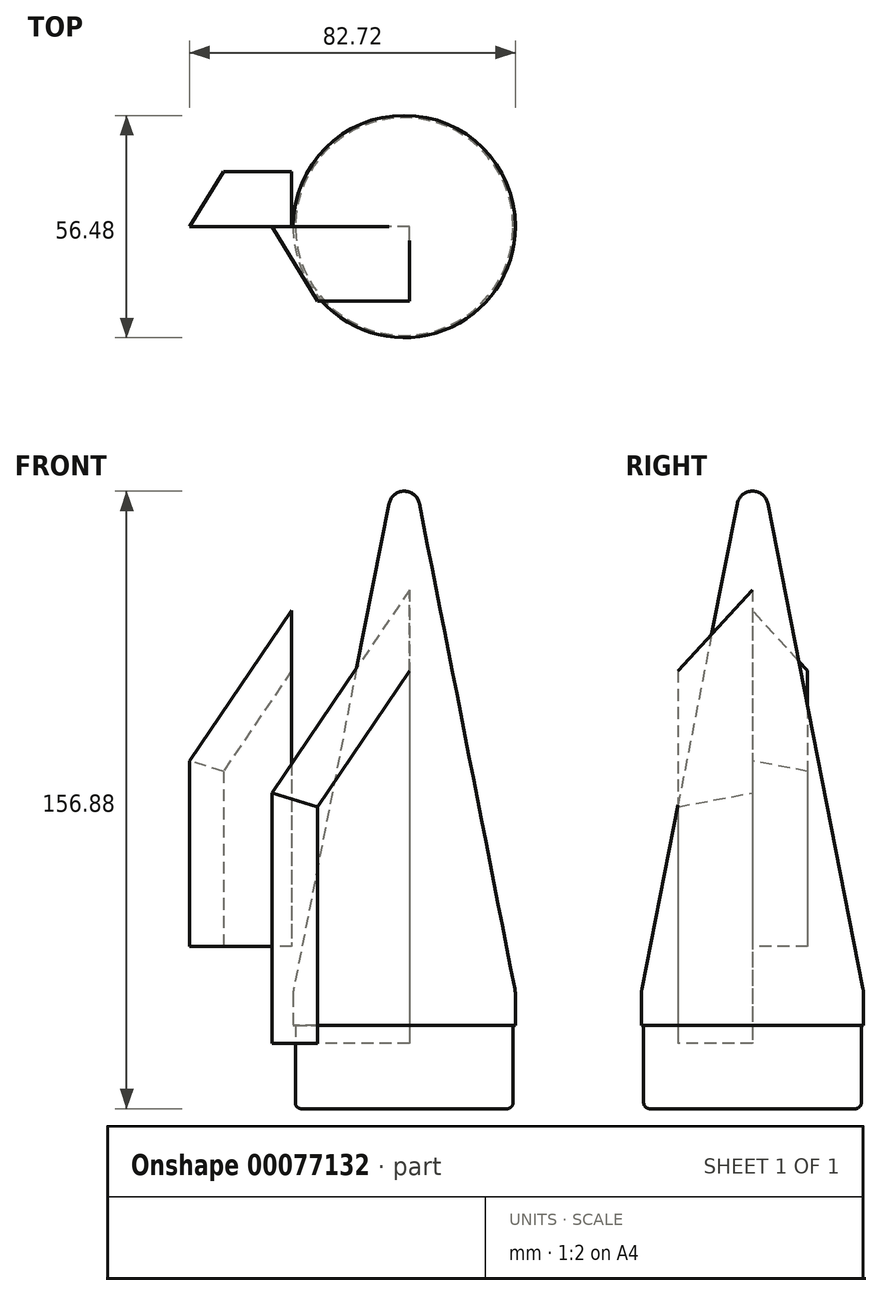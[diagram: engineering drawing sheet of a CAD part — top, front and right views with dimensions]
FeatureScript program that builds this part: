
annotation { "Feature Type Name" : "Feature", "Feature Type Description" : "" }
export const myFeature = defineFeature(function(context is Context, id is Id, definition is map)
    precondition{}
    {
        {
            var Q0;
            Q0=qCreatedBy(makeId("Front.planeOp"),FACE);
            var sketch = newSketch(context, id + "F0", { "sketchPlane" : qUnion([Q0])});
            skLineSegment(sketch, "E0", {"start": v(-33.3, -70.07) * mm, "end": v(-33.3, -70.07) * mm});
            skLineSegment(sketch, "E1", {"start": v(0, -70.07) * mm, "end": v(0, 79.93) * mm});
            skLineSegment(sketch, "E2", {"start": v(0, -70.07) * mm, "end": v(0, -80.07) * mm});
            skLineSegment(sketch, "E3", {"start": v(-32.6, -80.07) * mm, "end": v(-33.3, -80.07) * mm});
            skLineSegment(sketch, "E4", {"start": v(-33.3, -80.07) * mm, "end": v(-33.3, -70.07) * mm});
            skPoint(sketch, "E5.orphan", {"position": v(0, 86.63) * mm});
            skLineSegment(sketch, "E6", {"start": v(-33.3, -70.07) * mm, "end": v(-4.56, 76.18) * mm});
            skLineSegment(sketch, "E7.top", {"start": v(0, -105.07) * mm, "end": v(-32.6, -105.07) * mm});
            skLineSegment(sketch, "E7.left", {"start": v(0, -80.07) * mm, "end": v(0, -105.07) * mm});
            skLineSegment(sketch, "E7.right", {"start": v(-32.6, -80.07) * mm, "end": v(-32.6, -105.07) * mm});
            skArc(sketch, "E8", {"start": v(0, 79.93) * mm, "mid": v(-2.95, 78.87) * mm, "end": v(-4.56, 76.18) * mm});
            skSolve(sketch);
        }
        {
            var Q0;
            {var subQ0=sQuery(id+"F0.wireOp",EDGE,"E2");Q0=makeQuery(id+"F0.imprint","IMPRINT",FACE,{"disambiguationData":[TD([[makeQuery(id+"F0.imprint","IMPRINT",EDGE,{"derivedFrom":subQ0}),-1.0]])]});}
            var Q1;
            Q1=sQuery(id+"F0.wireOp",EDGE,"E1");
            revolve(context, id + "F1", {"entities" : qUnion([Q0]), "axis" : qUnion([Q1]), "revolveType" : RevolveType.FULL});
        }
        {
            var Q0;
            Q0=makeQuery(id+"F1.opRevolve","SWEPT_BODY",BODY,{"disambiguationData":[OSD([sQuery(id+"F0.wireOp",EDGE,"Oh61cgLR-RQo2-T4aV-TcRg-Gp7ijPdUG9jl"),sQuery(id+"F0.wireOp",EDGE,"E1"),sQuery(id+"F0.wireOp",EDGE,"E2"),sQuery(id+"F0.wireOp",EDGE,"E3"),sQuery(id+"F0.wireOp",EDGE,"E4"),sQuery(id+"F0.wireOp",EDGE,"E0"),sQuery(id+"F0.wireOp",EDGE,"dTV1AxgJ-VMAe-DLQO-Zqz3-4UbtDb8FiUJC")])]});
            var Q1;
            Q1=qCreatedBy(makeId("Origin.pointOp"),VERTEX);
            transform(context, id + "F2", {"entities" : qUnion([Q0]), "transformType" : TransformType.SCALE_UNIFORMLY, "scale" : .848, "scalePoint" : qUnion([Q1]), "makeCopy" : false});
        }
        {
            var Q0;
            Q0=qCreatedBy(makeId("Front.planeOp"),FACE);
            var sketch = newSketch(context, id + "F3", { "sketchPlane" : qUnion([Q0])});
            skLineSegment(sketch, "E9", {"start": v(-56.93, -47.9) * mm, "end": v(-56.93, 0) * mm});
            skLineSegment(sketch, "E10", {"start": v(-56.93, 0) * mm, "end": v(-28.6, 41.78) * mm});
            skLineSegment(sketch, "E11", {"start": v(-28.6, 41.78) * mm, "end": v(-28.6, -47.9) * mm});
            skLineSegment(sketch, "E12", {"start": v(-28.6, -47.9) * mm, "end": v(-56.93, -47.9) * mm});
            skSolve(sketch);
        }
        {
            var Q0;
            Q0=makeQuery(id+"F3.imprint","IMPRINT",FACE,{"disambiguationData":[TD([[makeQuery(id+"F3.imprint","IMPRINT",EDGE,{"derivedFrom":sQuery(id+"F3.wireOp",EDGE,"E9")}),-1.0]])]});
            extrude(context, id + "F4", {"entities" : qUnion([Q0]), "depth" : 14 * mm, "offsetDistance" : 25 * mm});
        }
        {
            var Q0;
            Q0=makeQuery(id+"F4.opExtrude","CAP_EDGE",EDGE,{"disambiguationData":[OSD([sQuery(id+"F3.wireOp",EDGE,"E10")])],"isStart":false});
            var Q1;
            Q1=makeQuery(id+"F4.opExtrude","CAP_EDGE",EDGE,{"disambiguationData":[OSD([sQuery(id+"F3.wireOp",EDGE,"E9")])],"isStart":false});
            chamfer(context, id + "F5", {"entities" : qUnion([Q0, Q1]), "chamferType" : ChamferType.TWO_OFFSETS, "width1" : 11 * mm, "oppositeDirection" : false, "width2" : 18 * mm, "tangentPropagation" : true});
        }
        {
            var Q0;
            Q0=makeQuery(id+"F4.opExtrude","SWEPT_BODY",BODY,{"disambiguationData":[OSD([sQuery(id+"F3.wireOp",EDGE,"E9"),sQuery(id+"F3.wireOp",EDGE,"E10"),sQuery(id+"F3.wireOp",EDGE,"E11"),sQuery(id+"F3.wireOp",EDGE,"E12")])]});
            var Q1;
            Q1=qCreatedBy(makeId("Front.planeOp"),FACE);
            mirror(context, id + "F6", {"operationType" : NewBodyOperationType.ADD, "entities" : qUnion([Q0]), "mirrorPlane" : qUnion([Q1])});
        }
        {
            var Q0;
            Q0=makeQuery(id+"F4.opExtrude","SWEPT_BODY",BODY,{"disambiguationData":[OSD([sQuery(id+"F3.wireOp",EDGE,"E9"),sQuery(id+"F3.wireOp",EDGE,"E10"),sQuery(id+"F3.wireOp",EDGE,"E11"),sQuery(id+"F3.wireOp",EDGE,"E12")])]});
            transform(context, id + "F7", {"entities" : qUnion([Q0]), "transformType" : TransformType.TRANSLATION_3D, "dx" : 29.6 * mm, "dy" : 0 * mm, "dz" : -5.8 * mm, "makeCopy" : false});
        }
        {
            var Q0;
            Q0=makeQuery(id+"F1.opRevolve","SWEPT_EDGE",EDGE,{"disambiguationData":[OSD([sQuery(id+"F0.wireOp",EDGE,"E4"),sQuery(id+"F0.wireOp",EDGE,"E6")])]});
            fillet(context, id + "F8", {"entities" : qUnion([Q0]), "radius" : 7.8 * mm, "tangentPropagation" : true, "allowEdgeOverflow" : false});
        }
        {
            var Q0;
            Q0=makeQuery(id+"F1.opRevolve","SWEPT_EDGE",EDGE,{"disambiguationData":[OSD([sQuery(id+"F0.wireOp",EDGE,"E7.top"),sQuery(id+"F0.wireOp",EDGE,"E7.right")])]});
            fillet(context, id + "F9", {"entities" : qUnion([Q0]), "radius" : 1.5 * mm, "tangentPropagation" : true, "allowEdgeOverflow" : false});
        }
        {
            var Q0;
            Q0=qCreatedBy(makeId("Top.planeOp"),FACE);
            cPlane(context, id + "F10", {"entities" : qUnion([Q0]), "cplaneType" : CPlaneType.OFFSET, "offset" : 25 * mm, "oppositeDirection" : true, "width" : 150 * mm, "height" : 150 * mm});
        }
        {
            var Q0;
            Q0=qCreatedBy(makeId("Front.planeOp"),FACE);
            cPlane(context, id + "F11", {"entities" : qUnion([Q0]), "cplaneType" : CPlaneType.OFFSET, "offset" : 35 * mm, "width" : 150 * mm, "height" : 150 * mm});
        }
        {
            var Q0;
            Q0=qCreatedBy(id+"F11.planeOp",FACE);
            var sketch = newSketch(context, id + "F12", { "sketchPlane" : qUnion([Q0])});
            skText(sketch, "E13", { "text": "DC3Dparts", "fontName": "OpenSans-Regular.ttf"});
            const initialGuessF12  = {"E13": [-0.024, -0.07859, 1, 0, 0.007]};
            skSetInitialGuess(sketch, initialGuessF12);
            skSolve(sketch);
        }
        {
            var Q0;
            Q0=qSketchRegion(id+"F12",true);
            var Q1;
            Q1=qCreatedBy(makeId("Front.planeOp"),FACE);
            extrude(context, id + "F13", {"entities" : qUnion([Q0]), "endBound" : BoundingType.UP_TO_SURFACE, "oppositeDirection" : true, "depth" : 25 * mm, "endBoundEntityFace" : qUnion([Q1]), "offsetDistance" : 25 * mm});
        }
        {
            var Q0;
            Q0=qCreatedBy(makeId("Front.planeOp"),FACE);
            var sketch = newSketch(context, id + "F14", { "sketchPlane" : qUnion([Q0])});
            skLineSegment(sketch, "E14.bottom", {"start": v(0, -64.71) * mm, "end": v(-27, -64.71) * mm});
            skLineSegment(sketch, "E14.top", {"start": v(0, -103.72) * mm, "end": v(-27, -103.72) * mm});
            skLineSegment(sketch, "E14.left", {"start": v(0, -64.71) * mm, "end": v(0, -103.72) * mm});
            skLineSegment(sketch, "E14.right", {"start": v(-27, -64.71) * mm, "end": v(-27, -103.72) * mm});
            skSolve(sketch);
        }
        {
            var Q0;
            Q0=makeQuery(id+"F14.imprint","IMPRINT",FACE,{"disambiguationData":[TD([[makeQuery(id+"F14.imprint","IMPRINT",EDGE,{"derivedFrom":sQuery(id+"F14.wireOp",EDGE,"E14.bottom")}),1.0]])]});
            var Q1;
            Q1=sQuery(id+"F14.wireOp",EDGE,"E14.left");
            revolve(context, id + "F15", {"entities" : qUnion([Q0]), "axis" : qUnion([Q1]), "revolveType" : RevolveType.FULL});
        }
        {
            var Q0;
            Q0=makeQuery(id+"F15.opRevolve","SWEPT_BODY",BODY,{"disambiguationData":[OSD([sQuery(id+"F14.wireOp",EDGE,"E14.bottom"),sQuery(id+"F14.wireOp",EDGE,"E14.top"),sQuery(id+"F14.wireOp",EDGE,"E14.left"),sQuery(id+"F14.wireOp",EDGE,"E14.right")])]});
            var Q1;
            Q1=makeQuery(id+"F13.opExtrude","SWEPT_BODY",BODY,{"disambiguationData":[OSD([sQuery(id+"F12.wireOp",EDGE,"E13.sketch_text.stroke-0"),sQuery(id+"F12.wireOp",EDGE,"E13.sketch_text.stroke-1"),sQuery(id+"F12.wireOp",EDGE,"E13.sketch_text.stroke-2"),sQuery(id+"F12.wireOp",EDGE,"E13.sketch_text.stroke-3"),sQuery(id+"F12.wireOp",EDGE,"E13.sketch_text.stroke-4"),sQuery(id+"F12.wireOp",EDGE,"E13.sketch_text.stroke-5"),sQuery(id+"F12.wireOp",EDGE,"E13.sketch_text.stroke-6"),sQuery(id+"F12.wireOp",EDGE,"E13.sketch_text.stroke-7"),sQuery(id+"F12.wireOp",EDGE,"E13.sketch_text.stroke-8"),sQuery(id+"F12.wireOp",EDGE,"E13.sketch_text.stroke-9"),sQuery(id+"F12.wireOp",EDGE,"E13.sketch_text.stroke-10"),sQuery(id+"F12.wireOp",EDGE,"E13.sketch_text.stroke-11"),sQuery(id+"F12.wireOp",EDGE,"E13.sketch_text.stroke-12"),sQuery(id+"F12.wireOp",EDGE,"E13.sketch_text.stroke-13")])]});
            var Q2;
            Q2=makeQuery(id+"F13.opExtrude","SWEPT_BODY",BODY,{"disambiguationData":[OSD([sQuery(id+"F12.wireOp",EDGE,"E13.sketch_text.stroke-14"),sQuery(id+"F12.wireOp",EDGE,"E13.sketch_text.stroke-15"),sQuery(id+"F12.wireOp",EDGE,"E13.sketch_text.stroke-16"),sQuery(id+"F12.wireOp",EDGE,"E13.sketch_text.stroke-17"),sQuery(id+"F12.wireOp",EDGE,"E13.sketch_text.stroke-18"),sQuery(id+"F12.wireOp",EDGE,"E13.sketch_text.stroke-19"),sQuery(id+"F12.wireOp",EDGE,"E13.sketch_text.stroke-20"),sQuery(id+"F12.wireOp",EDGE,"E13.sketch_text.stroke-21"),sQuery(id+"F12.wireOp",EDGE,"E13.sketch_text.stroke-22"),sQuery(id+"F12.wireOp",EDGE,"E13.sketch_text.stroke-23"),sQuery(id+"F12.wireOp",EDGE,"E13.sketch_text.stroke-24"),sQuery(id+"F12.wireOp",EDGE,"E13.sketch_text.stroke-25"),sQuery(id+"F12.wireOp",EDGE,"E13.sketch_text.stroke-26"),sQuery(id+"F12.wireOp",EDGE,"E13.sketch_text.stroke-27"),sQuery(id+"F12.wireOp",EDGE,"E13.sketch_text.stroke-28")])]});
            var Q3;
            Q3=makeQuery(id+"F13.opExtrude","SWEPT_BODY",BODY,{"disambiguationData":[OSD([sQuery(id+"F12.wireOp",EDGE,"E13.sketch_text.stroke-29"),sQuery(id+"F12.wireOp",EDGE,"E13.sketch_text.stroke-30"),sQuery(id+"F12.wireOp",EDGE,"E13.sketch_text.stroke-31"),sQuery(id+"F12.wireOp",EDGE,"E13.sketch_text.stroke-32"),sQuery(id+"F12.wireOp",EDGE,"E13.sketch_text.stroke-33"),sQuery(id+"F12.wireOp",EDGE,"E13.sketch_text.stroke-34"),sQuery(id+"F12.wireOp",EDGE,"E13.sketch_text.stroke-35"),sQuery(id+"F12.wireOp",EDGE,"E13.sketch_text.stroke-36"),sQuery(id+"F12.wireOp",EDGE,"E13.sketch_text.stroke-37"),sQuery(id+"F12.wireOp",EDGE,"E13.sketch_text.stroke-38"),sQuery(id+"F12.wireOp",EDGE,"E13.sketch_text.stroke-39"),sQuery(id+"F12.wireOp",EDGE,"E13.sketch_text.stroke-40"),sQuery(id+"F12.wireOp",EDGE,"E13.sketch_text.stroke-41"),sQuery(id+"F12.wireOp",EDGE,"E13.sketch_text.stroke-42"),sQuery(id+"F12.wireOp",EDGE,"E13.sketch_text.stroke-43"),sQuery(id+"F12.wireOp",EDGE,"E13.sketch_text.stroke-44"),sQuery(id+"F12.wireOp",EDGE,"E13.sketch_text.stroke-45"),sQuery(id+"F12.wireOp",EDGE,"E13.sketch_text.stroke-46"),sQuery(id+"F12.wireOp",EDGE,"E13.sketch_text.stroke-47"),sQuery(id+"F12.wireOp",EDGE,"E13.sketch_text.stroke-48"),sQuery(id+"F12.wireOp",EDGE,"E13.sketch_text.stroke-49"),sQuery(id+"F12.wireOp",EDGE,"E13.sketch_text.stroke-50"),sQuery(id+"F12.wireOp",EDGE,"E13.sketch_text.stroke-51"),sQuery(id+"F12.wireOp",EDGE,"E13.sketch_text.stroke-52"),sQuery(id+"F12.wireOp",EDGE,"E13.sketch_text.stroke-53"),sQuery(id+"F12.wireOp",EDGE,"E13.sketch_text.stroke-54"),sQuery(id+"F12.wireOp",EDGE,"E13.sketch_text.stroke-55"),sQuery(id+"F12.wireOp",EDGE,"E13.sketch_text.stroke-56")])]});
            var Q4;
            Q4=makeQuery(id+"F13.opExtrude","SWEPT_BODY",BODY,{"disambiguationData":[OSD([sQuery(id+"F12.wireOp",EDGE,"E13.sketch_text.stroke-57"),sQuery(id+"F12.wireOp",EDGE,"E13.sketch_text.stroke-58"),sQuery(id+"F12.wireOp",EDGE,"E13.sketch_text.stroke-59"),sQuery(id+"F12.wireOp",EDGE,"E13.sketch_text.stroke-60"),sQuery(id+"F12.wireOp",EDGE,"E13.sketch_text.stroke-61"),sQuery(id+"F12.wireOp",EDGE,"E13.sketch_text.stroke-62"),sQuery(id+"F12.wireOp",EDGE,"E13.sketch_text.stroke-63"),sQuery(id+"F12.wireOp",EDGE,"E13.sketch_text.stroke-64"),sQuery(id+"F12.wireOp",EDGE,"E13.sketch_text.stroke-65"),sQuery(id+"F12.wireOp",EDGE,"E13.sketch_text.stroke-66"),sQuery(id+"F12.wireOp",EDGE,"E13.sketch_text.stroke-67"),sQuery(id+"F12.wireOp",EDGE,"E13.sketch_text.stroke-68"),sQuery(id+"F12.wireOp",EDGE,"E13.sketch_text.stroke-69"),sQuery(id+"F12.wireOp",EDGE,"E13.sketch_text.stroke-70")])]});
            var Q5;
            Q5=makeQuery(id+"F13.opExtrude","SWEPT_BODY",BODY,{"disambiguationData":[OSD([sQuery(id+"F12.wireOp",EDGE,"E13.sketch_text.stroke-71"),sQuery(id+"F12.wireOp",EDGE,"E13.sketch_text.stroke-72"),sQuery(id+"F12.wireOp",EDGE,"E13.sketch_text.stroke-73"),sQuery(id+"F12.wireOp",EDGE,"E13.sketch_text.stroke-74"),sQuery(id+"F12.wireOp",EDGE,"E13.sketch_text.stroke-75"),sQuery(id+"F12.wireOp",EDGE,"E13.sketch_text.stroke-76"),sQuery(id+"F12.wireOp",EDGE,"E13.sketch_text.stroke-77"),sQuery(id+"F12.wireOp",EDGE,"E13.sketch_text.stroke-78"),sQuery(id+"F12.wireOp",EDGE,"E13.sketch_text.stroke-79"),sQuery(id+"F12.wireOp",EDGE,"E13.sketch_text.stroke-80"),sQuery(id+"F12.wireOp",EDGE,"E13.sketch_text.stroke-81"),sQuery(id+"F12.wireOp",EDGE,"E13.sketch_text.stroke-82"),sQuery(id+"F12.wireOp",EDGE,"E13.sketch_text.stroke-83"),sQuery(id+"F12.wireOp",EDGE,"E13.sketch_text.stroke-84"),sQuery(id+"F12.wireOp",EDGE,"E13.sketch_text.stroke-85"),sQuery(id+"F12.wireOp",EDGE,"E13.sketch_text.stroke-86"),sQuery(id+"F12.wireOp",EDGE,"E13.sketch_text.stroke-87"),sQuery(id+"F12.wireOp",EDGE,"E13.sketch_text.stroke-88"),sQuery(id+"F12.wireOp",EDGE,"E13.sketch_text.stroke-89"),sQuery(id+"F12.wireOp",EDGE,"E13.sketch_text.stroke-90"),sQuery(id+"F12.wireOp",EDGE,"E13.sketch_text.stroke-91"),sQuery(id+"F12.wireOp",EDGE,"E13.sketch_text.stroke-92"),sQuery(id+"F12.wireOp",EDGE,"E13.sketch_text.stroke-93"),sQuery(id+"F12.wireOp",EDGE,"E13.sketch_text.stroke-94"),sQuery(id+"F12.wireOp",EDGE,"E13.sketch_text.stroke-95")])]});
            var Q6;
            Q6=makeQuery(id+"F13.opExtrude","SWEPT_BODY",BODY,{"disambiguationData":[OSD([sQuery(id+"F12.wireOp",EDGE,"E13.sketch_text.stroke-96"),sQuery(id+"F12.wireOp",EDGE,"E13.sketch_text.stroke-97"),sQuery(id+"F12.wireOp",EDGE,"E13.sketch_text.stroke-98"),sQuery(id+"F12.wireOp",EDGE,"E13.sketch_text.stroke-99"),sQuery(id+"F12.wireOp",EDGE,"E13.sketch_text.stroke-100"),sQuery(id+"F12.wireOp",EDGE,"E13.sketch_text.stroke-101"),sQuery(id+"F12.wireOp",EDGE,"E13.sketch_text.stroke-102"),sQuery(id+"F12.wireOp",EDGE,"E13.sketch_text.stroke-103"),sQuery(id+"F12.wireOp",EDGE,"E13.sketch_text.stroke-104"),sQuery(id+"F12.wireOp",EDGE,"E13.sketch_text.stroke-105"),sQuery(id+"F12.wireOp",EDGE,"E13.sketch_text.stroke-106"),sQuery(id+"F12.wireOp",EDGE,"E13.sketch_text.stroke-107"),sQuery(id+"F12.wireOp",EDGE,"E13.sketch_text.stroke-108"),sQuery(id+"F12.wireOp",EDGE,"E13.sketch_text.stroke-109"),sQuery(id+"F12.wireOp",EDGE,"E13.sketch_text.stroke-110"),sQuery(id+"F12.wireOp",EDGE,"E13.sketch_text.stroke-111"),sQuery(id+"F12.wireOp",EDGE,"E13.sketch_text.stroke-112"),sQuery(id+"F12.wireOp",EDGE,"E13.sketch_text.stroke-113"),sQuery(id+"F12.wireOp",EDGE,"E13.sketch_text.stroke-114"),sQuery(id+"F12.wireOp",EDGE,"E13.sketch_text.stroke-115"),sQuery(id+"F12.wireOp",EDGE,"E13.sketch_text.stroke-116"),sQuery(id+"F12.wireOp",EDGE,"E13.sketch_text.stroke-117"),sQuery(id+"F12.wireOp",EDGE,"E13.sketch_text.stroke-118"),sQuery(id+"F12.wireOp",EDGE,"E13.sketch_text.stroke-119"),sQuery(id+"F12.wireOp",EDGE,"E13.sketch_text.stroke-120"),sQuery(id+"F12.wireOp",EDGE,"E13.sketch_text.stroke-121"),sQuery(id+"F12.wireOp",EDGE,"E13.sketch_text.stroke-122")])]});
            var Q7;
            Q7=makeQuery(id+"F13.opExtrude","SWEPT_BODY",BODY,{"disambiguationData":[OSD([sQuery(id+"F12.wireOp",EDGE,"E13.sketch_text.stroke-123"),sQuery(id+"F12.wireOp",EDGE,"E13.sketch_text.stroke-124"),sQuery(id+"F12.wireOp",EDGE,"E13.sketch_text.stroke-125"),sQuery(id+"F12.wireOp",EDGE,"E13.sketch_text.stroke-126"),sQuery(id+"F12.wireOp",EDGE,"E13.sketch_text.stroke-127"),sQuery(id+"F12.wireOp",EDGE,"E13.sketch_text.stroke-128"),sQuery(id+"F12.wireOp",EDGE,"E13.sketch_text.stroke-129"),sQuery(id+"F12.wireOp",EDGE,"E13.sketch_text.stroke-130"),sQuery(id+"F12.wireOp",EDGE,"E13.sketch_text.stroke-131"),sQuery(id+"F12.wireOp",EDGE,"E13.sketch_text.stroke-132"),sQuery(id+"F12.wireOp",EDGE,"E13.sketch_text.stroke-133"),sQuery(id+"F12.wireOp",EDGE,"E13.sketch_text.stroke-134"),sQuery(id+"F12.wireOp",EDGE,"E13.sketch_text.stroke-135")])]});
            var Q8;
            Q8=makeQuery(id+"F13.opExtrude","SWEPT_BODY",BODY,{"disambiguationData":[OSD([sQuery(id+"F12.wireOp",EDGE,"E13.sketch_text.stroke-136"),sQuery(id+"F12.wireOp",EDGE,"E13.sketch_text.stroke-137"),sQuery(id+"F12.wireOp",EDGE,"E13.sketch_text.stroke-138"),sQuery(id+"F12.wireOp",EDGE,"E13.sketch_text.stroke-139"),sQuery(id+"F12.wireOp",EDGE,"E13.sketch_text.stroke-140"),sQuery(id+"F12.wireOp",EDGE,"E13.sketch_text.stroke-141"),sQuery(id+"F12.wireOp",EDGE,"E13.sketch_text.stroke-142"),sQuery(id+"F12.wireOp",EDGE,"E13.sketch_text.stroke-143"),sQuery(id+"F12.wireOp",EDGE,"E13.sketch_text.stroke-144"),sQuery(id+"F12.wireOp",EDGE,"E13.sketch_text.stroke-145"),sQuery(id+"F12.wireOp",EDGE,"E13.sketch_text.stroke-146"),sQuery(id+"F12.wireOp",EDGE,"E13.sketch_text.stroke-147"),sQuery(id+"F12.wireOp",EDGE,"E13.sketch_text.stroke-148"),sQuery(id+"F12.wireOp",EDGE,"E13.sketch_text.stroke-149"),sQuery(id+"F12.wireOp",EDGE,"E13.sketch_text.stroke-150"),sQuery(id+"F12.wireOp",EDGE,"E13.sketch_text.stroke-151"),sQuery(id+"F12.wireOp",EDGE,"E13.sketch_text.stroke-152"),sQuery(id+"F12.wireOp",EDGE,"E13.sketch_text.stroke-153"),sQuery(id+"F12.wireOp",EDGE,"E13.sketch_text.stroke-154")])]});
            var Q9;
            Q9=makeQuery(id+"F13.opExtrude","SWEPT_BODY",BODY,{"disambiguationData":[OSD([sQuery(id+"F12.wireOp",EDGE,"E13.sketch_text.stroke-155"),sQuery(id+"F12.wireOp",EDGE,"E13.sketch_text.stroke-156"),sQuery(id+"F12.wireOp",EDGE,"E13.sketch_text.stroke-157"),sQuery(id+"F12.wireOp",EDGE,"E13.sketch_text.stroke-158"),sQuery(id+"F12.wireOp",EDGE,"E13.sketch_text.stroke-159"),sQuery(id+"F12.wireOp",EDGE,"E13.sketch_text.stroke-160"),sQuery(id+"F12.wireOp",EDGE,"E13.sketch_text.stroke-161"),sQuery(id+"F12.wireOp",EDGE,"E13.sketch_text.stroke-162"),sQuery(id+"F12.wireOp",EDGE,"E13.sketch_text.stroke-163"),sQuery(id+"F12.wireOp",EDGE,"E13.sketch_text.stroke-164"),sQuery(id+"F12.wireOp",EDGE,"E13.sketch_text.stroke-165"),sQuery(id+"F12.wireOp",EDGE,"E13.sketch_text.stroke-166"),sQuery(id+"F12.wireOp",EDGE,"E13.sketch_text.stroke-167"),sQuery(id+"F12.wireOp",EDGE,"E13.sketch_text.stroke-168"),sQuery(id+"F12.wireOp",EDGE,"E13.sketch_text.stroke-169"),sQuery(id+"F12.wireOp",EDGE,"E13.sketch_text.stroke-170"),sQuery(id+"F12.wireOp",EDGE,"E13.sketch_text.stroke-171"),sQuery(id+"F12.wireOp",EDGE,"E13.sketch_text.stroke-172"),sQuery(id+"F12.wireOp",EDGE,"E13.sketch_text.stroke-173"),sQuery(id+"F12.wireOp",EDGE,"E13.sketch_text.stroke-174"),sQuery(id+"F12.wireOp",EDGE,"E13.sketch_text.stroke-175"),sQuery(id+"F12.wireOp",EDGE,"E13.sketch_text.stroke-176"),sQuery(id+"F12.wireOp",EDGE,"E13.sketch_text.stroke-177"),sQuery(id+"F12.wireOp",EDGE,"E13.sketch_text.stroke-178"),sQuery(id+"F12.wireOp",EDGE,"E13.sketch_text.stroke-179")])]});
            booleanBodies(context, id + "F16", {"operationType" : BooleanOperationType.SUBTRACTION, "tools" : qUnion([Q0]), "targets" : qUnion([Q1, Q2, Q3, Q4, Q5, Q6, Q7, Q8, Q9])});
        }
        {
            var Q0;
            Q0=makeQuery(id+"F13.opExtrude","SWEPT_BODY",BODY,{"disambiguationData":[OSD([sQuery(id+"F12.wireOp",EDGE,"E13.sketch_text.stroke-0"),sQuery(id+"F12.wireOp",EDGE,"E13.sketch_text.stroke-1"),sQuery(id+"F12.wireOp",EDGE,"E13.sketch_text.stroke-2"),sQuery(id+"F12.wireOp",EDGE,"E13.sketch_text.stroke-3"),sQuery(id+"F12.wireOp",EDGE,"E13.sketch_text.stroke-4"),sQuery(id+"F12.wireOp",EDGE,"E13.sketch_text.stroke-5"),sQuery(id+"F12.wireOp",EDGE,"E13.sketch_text.stroke-6"),sQuery(id+"F12.wireOp",EDGE,"E13.sketch_text.stroke-7"),sQuery(id+"F12.wireOp",EDGE,"E13.sketch_text.stroke-8"),sQuery(id+"F12.wireOp",EDGE,"E13.sketch_text.stroke-9"),sQuery(id+"F12.wireOp",EDGE,"E13.sketch_text.stroke-10"),sQuery(id+"F12.wireOp",EDGE,"E13.sketch_text.stroke-11"),sQuery(id+"F12.wireOp",EDGE,"E13.sketch_text.stroke-12"),sQuery(id+"F12.wireOp",EDGE,"E13.sketch_text.stroke-13")])]});
            var Q1;
            Q1=makeQuery(id+"F13.opExtrude","SWEPT_BODY",BODY,{"disambiguationData":[OSD([sQuery(id+"F12.wireOp",EDGE,"E13.sketch_text.stroke-14"),sQuery(id+"F12.wireOp",EDGE,"E13.sketch_text.stroke-15"),sQuery(id+"F12.wireOp",EDGE,"E13.sketch_text.stroke-16"),sQuery(id+"F12.wireOp",EDGE,"E13.sketch_text.stroke-17"),sQuery(id+"F12.wireOp",EDGE,"E13.sketch_text.stroke-18"),sQuery(id+"F12.wireOp",EDGE,"E13.sketch_text.stroke-19"),sQuery(id+"F12.wireOp",EDGE,"E13.sketch_text.stroke-20"),sQuery(id+"F12.wireOp",EDGE,"E13.sketch_text.stroke-21"),sQuery(id+"F12.wireOp",EDGE,"E13.sketch_text.stroke-22"),sQuery(id+"F12.wireOp",EDGE,"E13.sketch_text.stroke-23"),sQuery(id+"F12.wireOp",EDGE,"E13.sketch_text.stroke-24"),sQuery(id+"F12.wireOp",EDGE,"E13.sketch_text.stroke-25"),sQuery(id+"F12.wireOp",EDGE,"E13.sketch_text.stroke-26"),sQuery(id+"F12.wireOp",EDGE,"E13.sketch_text.stroke-27"),sQuery(id+"F12.wireOp",EDGE,"E13.sketch_text.stroke-28")])]});
            var Q2;
            Q2=makeQuery(id+"F13.opExtrude","SWEPT_BODY",BODY,{"disambiguationData":[OSD([sQuery(id+"F12.wireOp",EDGE,"E13.sketch_text.stroke-29"),sQuery(id+"F12.wireOp",EDGE,"E13.sketch_text.stroke-30"),sQuery(id+"F12.wireOp",EDGE,"E13.sketch_text.stroke-31"),sQuery(id+"F12.wireOp",EDGE,"E13.sketch_text.stroke-32"),sQuery(id+"F12.wireOp",EDGE,"E13.sketch_text.stroke-33"),sQuery(id+"F12.wireOp",EDGE,"E13.sketch_text.stroke-34"),sQuery(id+"F12.wireOp",EDGE,"E13.sketch_text.stroke-35"),sQuery(id+"F12.wireOp",EDGE,"E13.sketch_text.stroke-36"),sQuery(id+"F12.wireOp",EDGE,"E13.sketch_text.stroke-37"),sQuery(id+"F12.wireOp",EDGE,"E13.sketch_text.stroke-38"),sQuery(id+"F12.wireOp",EDGE,"E13.sketch_text.stroke-39"),sQuery(id+"F12.wireOp",EDGE,"E13.sketch_text.stroke-40"),sQuery(id+"F12.wireOp",EDGE,"E13.sketch_text.stroke-41"),sQuery(id+"F12.wireOp",EDGE,"E13.sketch_text.stroke-42"),sQuery(id+"F12.wireOp",EDGE,"E13.sketch_text.stroke-43"),sQuery(id+"F12.wireOp",EDGE,"E13.sketch_text.stroke-44"),sQuery(id+"F12.wireOp",EDGE,"E13.sketch_text.stroke-45"),sQuery(id+"F12.wireOp",EDGE,"E13.sketch_text.stroke-46"),sQuery(id+"F12.wireOp",EDGE,"E13.sketch_text.stroke-47"),sQuery(id+"F12.wireOp",EDGE,"E13.sketch_text.stroke-48"),sQuery(id+"F12.wireOp",EDGE,"E13.sketch_text.stroke-49"),sQuery(id+"F12.wireOp",EDGE,"E13.sketch_text.stroke-50"),sQuery(id+"F12.wireOp",EDGE,"E13.sketch_text.stroke-51"),sQuery(id+"F12.wireOp",EDGE,"E13.sketch_text.stroke-52"),sQuery(id+"F12.wireOp",EDGE,"E13.sketch_text.stroke-53"),sQuery(id+"F12.wireOp",EDGE,"E13.sketch_text.stroke-54"),sQuery(id+"F12.wireOp",EDGE,"E13.sketch_text.stroke-55"),sQuery(id+"F12.wireOp",EDGE,"E13.sketch_text.stroke-56")])]});
            var Q3;
            Q3=makeQuery(id+"F13.opExtrude","SWEPT_BODY",BODY,{"disambiguationData":[OSD([sQuery(id+"F12.wireOp",EDGE,"E13.sketch_text.stroke-57"),sQuery(id+"F12.wireOp",EDGE,"E13.sketch_text.stroke-58"),sQuery(id+"F12.wireOp",EDGE,"E13.sketch_text.stroke-59"),sQuery(id+"F12.wireOp",EDGE,"E13.sketch_text.stroke-60"),sQuery(id+"F12.wireOp",EDGE,"E13.sketch_text.stroke-61"),sQuery(id+"F12.wireOp",EDGE,"E13.sketch_text.stroke-62"),sQuery(id+"F12.wireOp",EDGE,"E13.sketch_text.stroke-63"),sQuery(id+"F12.wireOp",EDGE,"E13.sketch_text.stroke-64"),sQuery(id+"F12.wireOp",EDGE,"E13.sketch_text.stroke-65"),sQuery(id+"F12.wireOp",EDGE,"E13.sketch_text.stroke-66"),sQuery(id+"F12.wireOp",EDGE,"E13.sketch_text.stroke-67"),sQuery(id+"F12.wireOp",EDGE,"E13.sketch_text.stroke-68"),sQuery(id+"F12.wireOp",EDGE,"E13.sketch_text.stroke-69"),sQuery(id+"F12.wireOp",EDGE,"E13.sketch_text.stroke-70")])]});
            var Q4;
            Q4=makeQuery(id+"F13.opExtrude","SWEPT_BODY",BODY,{"disambiguationData":[OSD([sQuery(id+"F12.wireOp",EDGE,"E13.sketch_text.stroke-71"),sQuery(id+"F12.wireOp",EDGE,"E13.sketch_text.stroke-72"),sQuery(id+"F12.wireOp",EDGE,"E13.sketch_text.stroke-73"),sQuery(id+"F12.wireOp",EDGE,"E13.sketch_text.stroke-74"),sQuery(id+"F12.wireOp",EDGE,"E13.sketch_text.stroke-75"),sQuery(id+"F12.wireOp",EDGE,"E13.sketch_text.stroke-76"),sQuery(id+"F12.wireOp",EDGE,"E13.sketch_text.stroke-77"),sQuery(id+"F12.wireOp",EDGE,"E13.sketch_text.stroke-78"),sQuery(id+"F12.wireOp",EDGE,"E13.sketch_text.stroke-79"),sQuery(id+"F12.wireOp",EDGE,"E13.sketch_text.stroke-80"),sQuery(id+"F12.wireOp",EDGE,"E13.sketch_text.stroke-81"),sQuery(id+"F12.wireOp",EDGE,"E13.sketch_text.stroke-82"),sQuery(id+"F12.wireOp",EDGE,"E13.sketch_text.stroke-83"),sQuery(id+"F12.wireOp",EDGE,"E13.sketch_text.stroke-84"),sQuery(id+"F12.wireOp",EDGE,"E13.sketch_text.stroke-85"),sQuery(id+"F12.wireOp",EDGE,"E13.sketch_text.stroke-86"),sQuery(id+"F12.wireOp",EDGE,"E13.sketch_text.stroke-87"),sQuery(id+"F12.wireOp",EDGE,"E13.sketch_text.stroke-88"),sQuery(id+"F12.wireOp",EDGE,"E13.sketch_text.stroke-89"),sQuery(id+"F12.wireOp",EDGE,"E13.sketch_text.stroke-90"),sQuery(id+"F12.wireOp",EDGE,"E13.sketch_text.stroke-91"),sQuery(id+"F12.wireOp",EDGE,"E13.sketch_text.stroke-92"),sQuery(id+"F12.wireOp",EDGE,"E13.sketch_text.stroke-93"),sQuery(id+"F12.wireOp",EDGE,"E13.sketch_text.stroke-94"),sQuery(id+"F12.wireOp",EDGE,"E13.sketch_text.stroke-95")])]});
            var Q5;
            Q5=makeQuery(id+"F13.opExtrude","SWEPT_BODY",BODY,{"disambiguationData":[OSD([sQuery(id+"F12.wireOp",EDGE,"E13.sketch_text.stroke-96"),sQuery(id+"F12.wireOp",EDGE,"E13.sketch_text.stroke-97"),sQuery(id+"F12.wireOp",EDGE,"E13.sketch_text.stroke-98"),sQuery(id+"F12.wireOp",EDGE,"E13.sketch_text.stroke-99"),sQuery(id+"F12.wireOp",EDGE,"E13.sketch_text.stroke-100"),sQuery(id+"F12.wireOp",EDGE,"E13.sketch_text.stroke-101"),sQuery(id+"F12.wireOp",EDGE,"E13.sketch_text.stroke-102"),sQuery(id+"F12.wireOp",EDGE,"E13.sketch_text.stroke-103"),sQuery(id+"F12.wireOp",EDGE,"E13.sketch_text.stroke-104"),sQuery(id+"F12.wireOp",EDGE,"E13.sketch_text.stroke-105"),sQuery(id+"F12.wireOp",EDGE,"E13.sketch_text.stroke-106"),sQuery(id+"F12.wireOp",EDGE,"E13.sketch_text.stroke-107"),sQuery(id+"F12.wireOp",EDGE,"E13.sketch_text.stroke-108"),sQuery(id+"F12.wireOp",EDGE,"E13.sketch_text.stroke-109"),sQuery(id+"F12.wireOp",EDGE,"E13.sketch_text.stroke-110"),sQuery(id+"F12.wireOp",EDGE,"E13.sketch_text.stroke-111"),sQuery(id+"F12.wireOp",EDGE,"E13.sketch_text.stroke-112"),sQuery(id+"F12.wireOp",EDGE,"E13.sketch_text.stroke-113"),sQuery(id+"F12.wireOp",EDGE,"E13.sketch_text.stroke-114"),sQuery(id+"F12.wireOp",EDGE,"E13.sketch_text.stroke-115"),sQuery(id+"F12.wireOp",EDGE,"E13.sketch_text.stroke-116"),sQuery(id+"F12.wireOp",EDGE,"E13.sketch_text.stroke-117"),sQuery(id+"F12.wireOp",EDGE,"E13.sketch_text.stroke-118"),sQuery(id+"F12.wireOp",EDGE,"E13.sketch_text.stroke-119"),sQuery(id+"F12.wireOp",EDGE,"E13.sketch_text.stroke-120"),sQuery(id+"F12.wireOp",EDGE,"E13.sketch_text.stroke-121"),sQuery(id+"F12.wireOp",EDGE,"E13.sketch_text.stroke-122")])]});
            var Q6;
            Q6=makeQuery(id+"F13.opExtrude","SWEPT_BODY",BODY,{"disambiguationData":[OSD([sQuery(id+"F12.wireOp",EDGE,"E13.sketch_text.stroke-123"),sQuery(id+"F12.wireOp",EDGE,"E13.sketch_text.stroke-124"),sQuery(id+"F12.wireOp",EDGE,"E13.sketch_text.stroke-125"),sQuery(id+"F12.wireOp",EDGE,"E13.sketch_text.stroke-126"),sQuery(id+"F12.wireOp",EDGE,"E13.sketch_text.stroke-127"),sQuery(id+"F12.wireOp",EDGE,"E13.sketch_text.stroke-128"),sQuery(id+"F12.wireOp",EDGE,"E13.sketch_text.stroke-129"),sQuery(id+"F12.wireOp",EDGE,"E13.sketch_text.stroke-130"),sQuery(id+"F12.wireOp",EDGE,"E13.sketch_text.stroke-131"),sQuery(id+"F12.wireOp",EDGE,"E13.sketch_text.stroke-132"),sQuery(id+"F12.wireOp",EDGE,"E13.sketch_text.stroke-133"),sQuery(id+"F12.wireOp",EDGE,"E13.sketch_text.stroke-134"),sQuery(id+"F12.wireOp",EDGE,"E13.sketch_text.stroke-135")])]});
            var Q7;
            Q7=makeQuery(id+"F13.opExtrude","SWEPT_BODY",BODY,{"disambiguationData":[OSD([sQuery(id+"F12.wireOp",EDGE,"E13.sketch_text.stroke-136"),sQuery(id+"F12.wireOp",EDGE,"E13.sketch_text.stroke-137"),sQuery(id+"F12.wireOp",EDGE,"E13.sketch_text.stroke-138"),sQuery(id+"F12.wireOp",EDGE,"E13.sketch_text.stroke-139"),sQuery(id+"F12.wireOp",EDGE,"E13.sketch_text.stroke-140"),sQuery(id+"F12.wireOp",EDGE,"E13.sketch_text.stroke-141"),sQuery(id+"F12.wireOp",EDGE,"E13.sketch_text.stroke-142"),sQuery(id+"F12.wireOp",EDGE,"E13.sketch_text.stroke-143"),sQuery(id+"F12.wireOp",EDGE,"E13.sketch_text.stroke-144"),sQuery(id+"F12.wireOp",EDGE,"E13.sketch_text.stroke-145"),sQuery(id+"F12.wireOp",EDGE,"E13.sketch_text.stroke-146"),sQuery(id+"F12.wireOp",EDGE,"E13.sketch_text.stroke-147"),sQuery(id+"F12.wireOp",EDGE,"E13.sketch_text.stroke-148"),sQuery(id+"F12.wireOp",EDGE,"E13.sketch_text.stroke-149"),sQuery(id+"F12.wireOp",EDGE,"E13.sketch_text.stroke-150"),sQuery(id+"F12.wireOp",EDGE,"E13.sketch_text.stroke-151"),sQuery(id+"F12.wireOp",EDGE,"E13.sketch_text.stroke-152"),sQuery(id+"F12.wireOp",EDGE,"E13.sketch_text.stroke-153"),sQuery(id+"F12.wireOp",EDGE,"E13.sketch_text.stroke-154")])]});
            var Q8;
            Q8=makeQuery(id+"F13.opExtrude","SWEPT_BODY",BODY,{"disambiguationData":[OSD([sQuery(id+"F12.wireOp",EDGE,"E13.sketch_text.stroke-155"),sQuery(id+"F12.wireOp",EDGE,"E13.sketch_text.stroke-156"),sQuery(id+"F12.wireOp",EDGE,"E13.sketch_text.stroke-157"),sQuery(id+"F12.wireOp",EDGE,"E13.sketch_text.stroke-158"),sQuery(id+"F12.wireOp",EDGE,"E13.sketch_text.stroke-159"),sQuery(id+"F12.wireOp",EDGE,"E13.sketch_text.stroke-160"),sQuery(id+"F12.wireOp",EDGE,"E13.sketch_text.stroke-161"),sQuery(id+"F12.wireOp",EDGE,"E13.sketch_text.stroke-162"),sQuery(id+"F12.wireOp",EDGE,"E13.sketch_text.stroke-163"),sQuery(id+"F12.wireOp",EDGE,"E13.sketch_text.stroke-164"),sQuery(id+"F12.wireOp",EDGE,"E13.sketch_text.stroke-165"),sQuery(id+"F12.wireOp",EDGE,"E13.sketch_text.stroke-166"),sQuery(id+"F12.wireOp",EDGE,"E13.sketch_text.stroke-167"),sQuery(id+"F12.wireOp",EDGE,"E13.sketch_text.stroke-168"),sQuery(id+"F12.wireOp",EDGE,"E13.sketch_text.stroke-169"),sQuery(id+"F12.wireOp",EDGE,"E13.sketch_text.stroke-170"),sQuery(id+"F12.wireOp",EDGE,"E13.sketch_text.stroke-171"),sQuery(id+"F12.wireOp",EDGE,"E13.sketch_text.stroke-172"),sQuery(id+"F12.wireOp",EDGE,"E13.sketch_text.stroke-173"),sQuery(id+"F12.wireOp",EDGE,"E13.sketch_text.stroke-174"),sQuery(id+"F12.wireOp",EDGE,"E13.sketch_text.stroke-175"),sQuery(id+"F12.wireOp",EDGE,"E13.sketch_text.stroke-176"),sQuery(id+"F12.wireOp",EDGE,"E13.sketch_text.stroke-177"),sQuery(id+"F12.wireOp",EDGE,"E13.sketch_text.stroke-178"),sQuery(id+"F12.wireOp",EDGE,"E13.sketch_text.stroke-179")])]});
            var Q9;
            Q9=makeQuery(id+"F4.opExtrude","SWEPT_BODY",BODY,{"disambiguationData":[OSD([sQuery(id+"F3.wireOp",EDGE,"E9"),sQuery(id+"F3.wireOp",EDGE,"E10"),sQuery(id+"F3.wireOp",EDGE,"E11"),sQuery(id+"F3.wireOp",EDGE,"E12")])]});
            booleanBodies(context, id + "F17", {"operationType" : BooleanOperationType.SUBTRACTION, "tools" : qUnion([Q0, Q1, Q2, Q3, Q4, Q5, Q6, Q7, Q8]), "targets" : qUnion([Q9])});
        }
        {
            var Q0;
            Q0=qCreatedBy(id+"F10.planeOp",FACE);
            var sketch = newSketch(context, id + "F18", { "sketchPlane" : qUnion([Q0])});
            skCircle(sketch, "E15", {"center": v(0, 21.08) * mm, "radius": 2 * mm});
            skSolve(sketch);
        }
        {
            var Q0;
            Q0=makeQuery(id+"F18.imprint","IMPRINT",FACE,{"disambiguationData":[TD([[makeQuery(id+"F18.imprint","IMPRINT",EDGE,{"derivedFrom":sQuery(id+"F18.wireOp",EDGE,"E15")}),1.0]])]});
            extrude(context, id + "F19", {"entities" : qUnion([Q0]), "depth" : 25 * mm, "offsetDistance" : 25 * mm});
        }
        {
            var Q0;
            Q0=makeQuery(id+"F19.opExtrude","CAP_EDGE",EDGE,{"disambiguationData":[OSD([sQuery(id+"F18.wireOp",EDGE,"E15")])],"isStart":true});
            fillet(context, id + "F20", {"entities" : qUnion([Q0]), "radius" : 2 * mm, "tangentPropagation" : true, "allowEdgeOverflow" : false});
        }
        {
            var Q0;
            Q0=makeQuery(id+"F19.opExtrude","SWEPT_BODY",BODY,{"disambiguationData":[OSD([sQuery(id+"F18.wireOp",EDGE,"E15")])]});
            transform(context, id + "F21", {"entities" : qUnion([Q0]), "transformType" : TransformType.TRANSLATION_3D, "dx" : 16.4 * mm, "dy" : -4.8 * mm, "dz" : -10.6 * mm, "makeCopy" : true});
        }
        {
            var Q0;
            Q0=makeQuery(id+"F19.opExtrude","SWEPT_BODY",BODY,{"disambiguationData":[OSD([sQuery(id+"F18.wireOp",EDGE,"E15")])]});
            transform(context, id + "F22", {"entities" : qUnion([Q0]), "transformType" : TransformType.TRANSLATION_3D, "dx" : 8.3 * mm, "dy" : -1.9 * mm, "dz" : 0 * mm, "makeCopy" : false});
        }
        {
            var Q0;
            Q0=makeQuery(id+"F19.opExtrude","SWEPT_BODY",BODY,{"disambiguationData":[OSD([sQuery(id+"F18.wireOp",EDGE,"E15")])]});
            var Q1;
            Q1=makeQuery(id+"F21.opPattern","COPY",BODY,{"derivedFrom":makeQuery(id+"F19.opExtrude","SWEPT_BODY",BODY,{"disambiguationData":[OSD([sQuery(id+"F18.wireOp",EDGE,"E15")])]}),"instanceName":"1"});
            var Q2;
            Q2=qCreatedBy(makeId("Front.planeOp"),FACE);
            mirror(context, id + "F23", {"entities" : qUnion([Q0, Q1]), "mirrorPlane" : qUnion([Q2])});
        }
        {
            var Q0;
            Q0=makeQuery(id+"F19.opExtrude","SWEPT_BODY",BODY,{"disambiguationData":[OSD([sQuery(id+"F18.wireOp",EDGE,"E15")])]});
            var Q1;
            Q1=makeQuery(id+"F23.opPattern","COPY",BODY,{"derivedFrom":makeQuery(id+"F19.opExtrude","SWEPT_BODY",BODY,{"disambiguationData":[OSD([sQuery(id+"F18.wireOp",EDGE,"E15")])]}),"instanceName":"1"});
            var Q2;
            Q2=makeQuery(id+"F21.opPattern","COPY",BODY,{"derivedFrom":makeQuery(id+"F19.opExtrude","SWEPT_BODY",BODY,{"disambiguationData":[OSD([sQuery(id+"F18.wireOp",EDGE,"E15")])]}),"instanceName":"1"});
            var Q3;
            Q3=makeQuery(id+"F23.opPattern","COPY",BODY,{"derivedFrom":makeQuery(id+"F21.opPattern","COPY",BODY,{"derivedFrom":makeQuery(id+"F19.opExtrude","SWEPT_BODY",BODY,{"disambiguationData":[OSD([sQuery(id+"F18.wireOp",EDGE,"E15")])]}),"instanceName":"1"}),"instanceName":"1"});
            var Q4;
            Q4=makeQuery(id+"F4.opExtrude","SWEPT_BODY",BODY,{"disambiguationData":[OSD([sQuery(id+"F3.wireOp",EDGE,"E9"),sQuery(id+"F3.wireOp",EDGE,"E10"),sQuery(id+"F3.wireOp",EDGE,"E11"),sQuery(id+"F3.wireOp",EDGE,"E12")])]});
            booleanBodies(context, id + "F24", {"operationType" : BooleanOperationType.SUBTRACTION, "tools" : qUnion([Q0, Q1, Q2, Q3]), "targets" : qUnion([Q4])});
        }
        {
            var Q0;
            Q0=makeQuery(id+"F4.opExtrude","SWEPT_BODY",BODY,{"disambiguationData":[OSD([sQuery(id+"F3.wireOp",EDGE,"E9"),sQuery(id+"F3.wireOp",EDGE,"E10"),sQuery(id+"F3.wireOp",EDGE,"E11"),sQuery(id+"F3.wireOp",EDGE,"E12")])]});
            var Q1;
            Q1=qCreatedBy(makeId("Origin.pointOp"),VERTEX);
            transform(context, id + "F25", {"entities" : qUnion([Q0]), "transformType" : TransformType.SCALE_UNIFORMLY, "scale" : 1.35, "scalePoint" : qUnion([Q1]), "makeCopy" : false});
        }
    });
